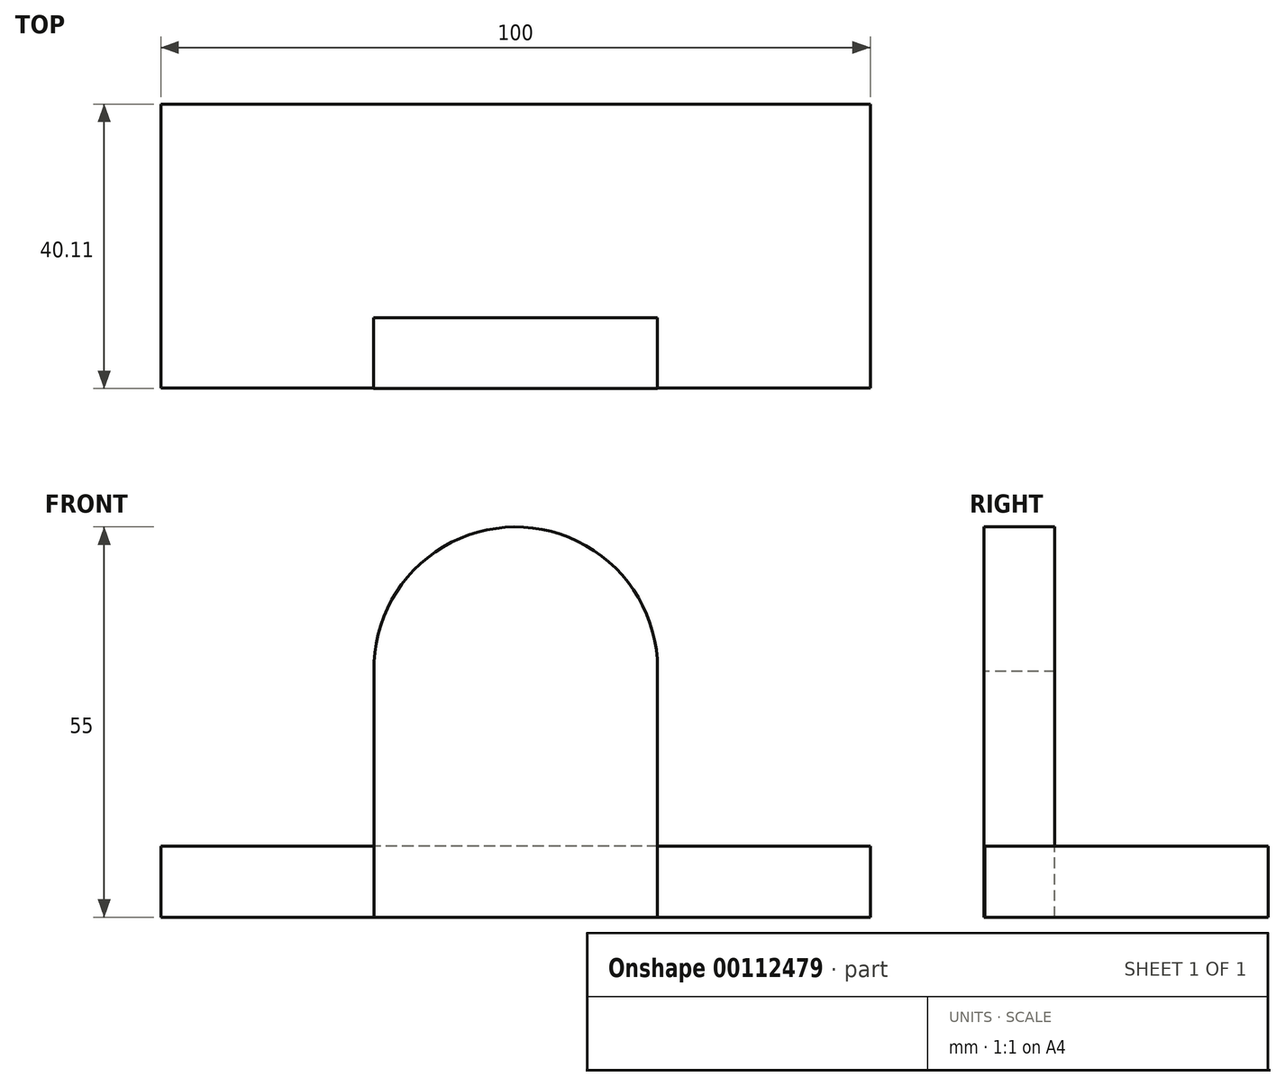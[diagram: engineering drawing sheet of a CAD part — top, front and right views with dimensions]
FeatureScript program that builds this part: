
annotation { "Feature Type Name" : "Feature", "Feature Type Description" : "" }
export const myFeature = defineFeature(function(context is Context, id is Id, definition is map)
    precondition{}
    {
        {
            var Q0;
            Q0=qCreatedBy(makeId("Top.planeOp"),FACE);
            var sketch = newSketch(context, id + "F0", { "sketchPlane" : qUnion([Q0])});
            skLineSegment(sketch, "E0.bottom", {"start": v(42.55, 0.1) * mm, "end": v(-57.45, 0.1) * mm});
            skLineSegment(sketch, "E0.top", {"start": v(42.55, 40.1) * mm, "end": v(-57.45, 40.1) * mm});
            skLineSegment(sketch, "E0.left", {"start": v(42.55, 0.1) * mm, "end": v(42.55, 40.1) * mm});
            skLineSegment(sketch, "E0.right", {"start": v(-57.45, 0.1) * mm, "end": v(-57.45, 40.1) * mm});
            skSolve(sketch);
        }
        {
            var Q0;
            Q0 = qSketchRegion(id + "F0", true);
            extrude(context, id + "F1", {"entities" : qUnion([Q0]), "depth" : 10 * mm});
        }
        {
            var Q0;
            Q0=qCreatedBy(makeId("Front.planeOp"),FACE);
            var sketch = newSketch(context, id + "F2", { "sketchPlane" : qUnion([Q0])});
            skLineSegment(sketch, "E1", {"start": v(-27.45, 0) * mm, "end": v(-27.45, 34.62) * mm});
            skLineSegment(sketch, "E2", {"start": v(12.55, 0) * mm, "end": v(12.55, 35) * mm});
            skArc(sketch, "E3", {"start": v(12.55, 35) * mm, "mid": v(-7.64, 55) * mm, "end": v(-27.45, 34.62) * mm});
            skLineSegment(sketch, "E4", {"start": v(12.55, 0) * mm, "end": v(-27.45, 0) * mm});
            skSolve(sketch);
        }
        {
            var Q0;
            Q0 = qSketchRegion(id + "F2", true);
            extrude(context, id + "F3", {"entities" : qUnion([Q0]), "oppositeDirection" : true, "depth" : 10 * mm});
        }
    });
